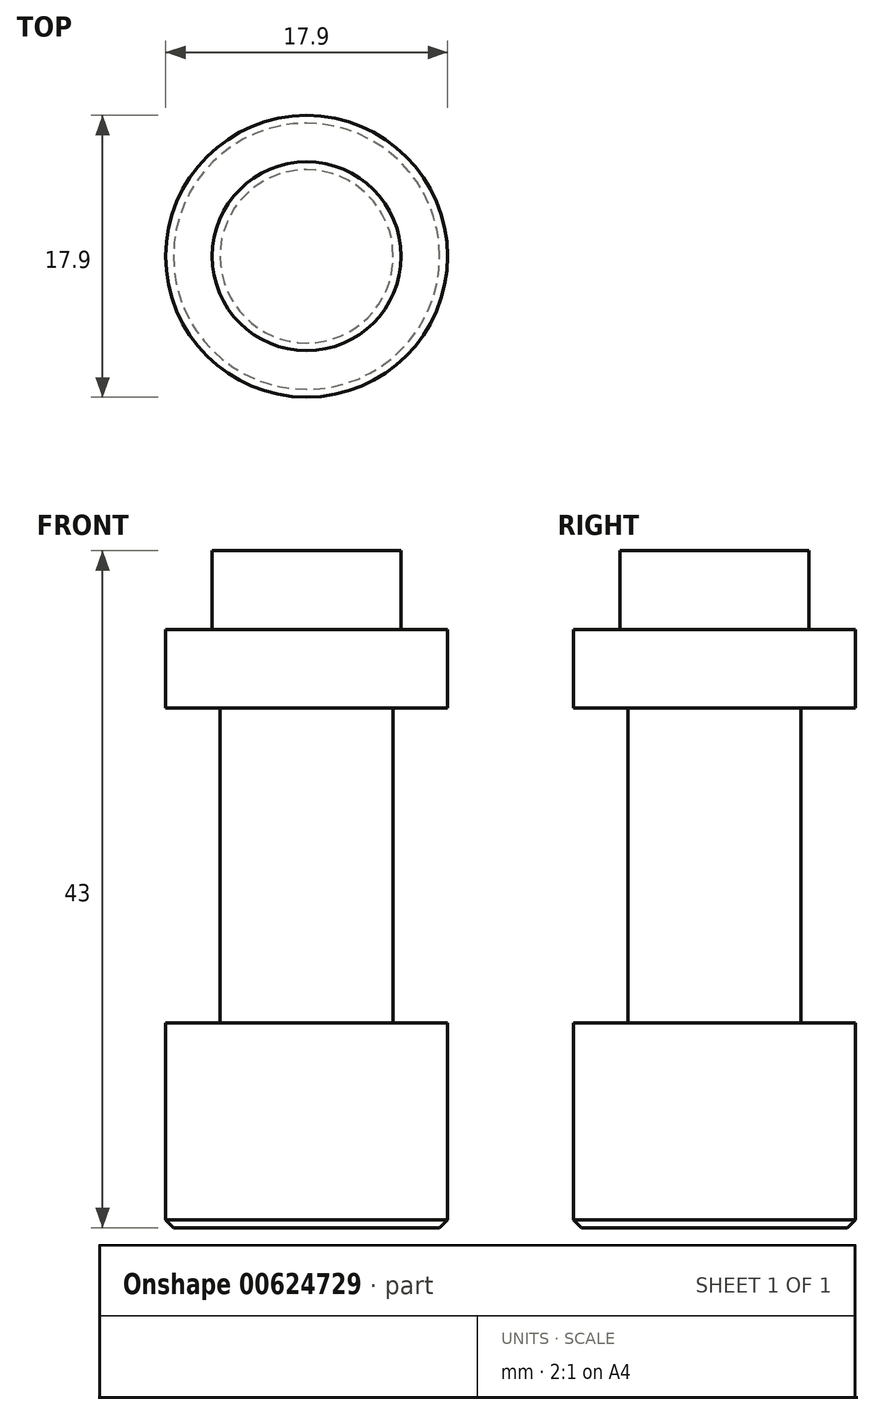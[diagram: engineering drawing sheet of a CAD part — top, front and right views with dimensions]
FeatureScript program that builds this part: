
annotation { "Feature Type Name" : "Feature", "Feature Type Description" : "" }
export const myFeature = defineFeature(function(context is Context, id is Id, definition is map)
    precondition{}
    {
        {
            var Q0;
            Q0=qCreatedBy(makeId("Front.planeOp"),FACE);
            var sketch = newSketch(context, id + "F0", { "sketchPlane" : qUnion([Q0])});
            skLineSegment(sketch, "E0", {"start": v(0, 0) * mm, "end": v(-8.45, 0) * mm});
            skLineSegment(sketch, "E1", {"start": v(-8.95, 0.5) * mm, "end": v(-8.95, 13) * mm});
            skLineSegment(sketch, "E2", {"start": v(-8.95, 13) * mm, "end": v(-5.5, 13) * mm});
            skLineSegment(sketch, "E3", {"start": v(-5.5, 13) * mm, "end": v(-5.5, 33) * mm});
            skLineSegment(sketch, "E4", {"start": v(-5.5, 33) * mm, "end": v(-8.95, 33) * mm});
            skLineSegment(sketch, "E5", {"start": v(-8.95, 33) * mm, "end": v(-8.95, 38) * mm});
            skLineSegment(sketch, "E6", {"start": v(-8.95, 38) * mm, "end": v(-6, 38) * mm});
            skLineSegment(sketch, "E7", {"start": v(-6, 38) * mm, "end": v(-6, 43) * mm});
            skLineSegment(sketch, "E8", {"start": v(-6, 43) * mm, "end": v(0, 43) * mm});
            skLineSegment(sketch, "E9", {"start": v(-8.95, 0.5) * mm, "end": v(-8.45, 0) * mm});
            skPoint(sketch, "E10.orphan", {"position": v(-8.95, 0) * mm});
            skLineSegment(sketch, "E11", {"start": v(0, 43) * mm, "end": v(0, 0) * mm});
            skSolve(sketch);
        }
        {
            var Q0;
            Q0 = qSketchRegion(id + "F0", true);
            var Q1;
            Q1=sQuery(id+"F0.wireOp",EDGE,"E11");
            revolve(context, id + "F1", {"entities" : qUnion([Q0]), "axis" : qUnion([Q1]), "revolveType" : RevolveType.FULL});
        }
    });
